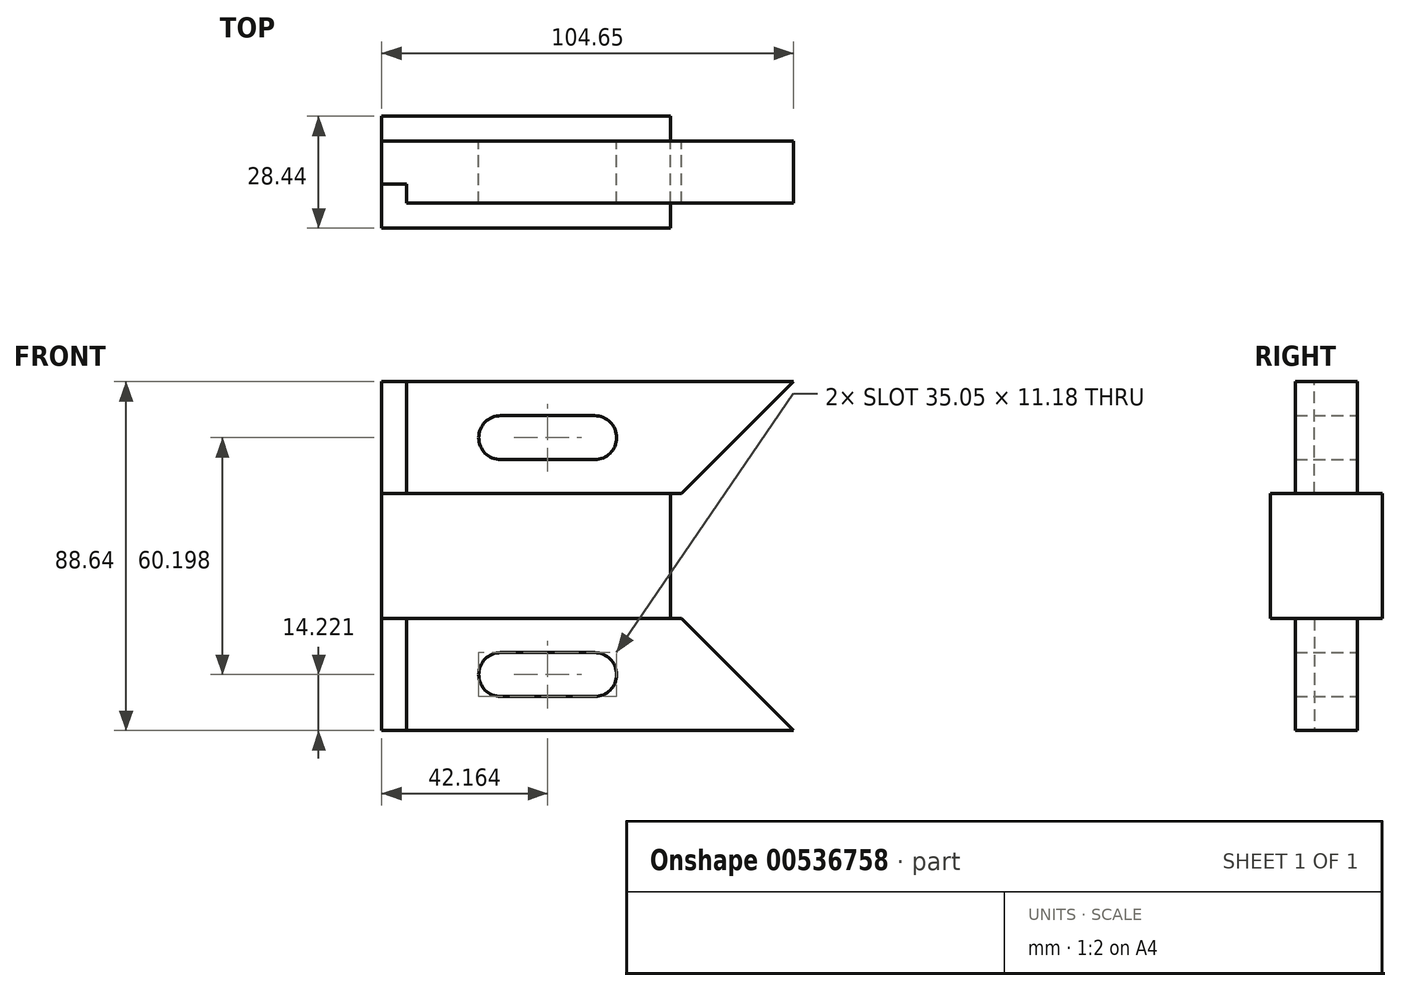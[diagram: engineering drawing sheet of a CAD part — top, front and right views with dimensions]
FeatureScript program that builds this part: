
annotation { "Feature Type Name" : "Feature", "Feature Type Description" : "" }
export const myFeature = defineFeature(function(context is Context, id is Id, definition is map)
    precondition{}
    {
        {
            var Q0;
            Q0=qCreatedBy(makeId("Right.planeOp"),FACE);
            var sketch = newSketch(context, id + "F0", { "sketchPlane" : qUnion([Q0])});
            skLineSegment(sketch, "E0.bottom", {"start": v(-14.22, 15.88) * mm, "end": v(14.22, 15.88) * mm});
            skLineSegment(sketch, "E0.top", {"start": v(-14.22, -15.87) * mm, "end": v(14.22, -15.87) * mm});
            skLineSegment(sketch, "E0.left", {"start": v(-14.22, 15.88) * mm, "end": v(-14.22, -15.88) * mm});
            skLineSegment(sketch, "E0.right", {"start": v(14.22, 15.88) * mm, "end": v(14.22, -15.88) * mm});
            skPoint(sketch, "E0.middle", {"position": v(0, 0) * mm});
            skSolve(sketch);
        }
        {
            var Q0;
            Q0=makeQuery(id+"F0.imprint","IMPRINT",FACE,{"disambiguationData":[TD([[makeQuery(id+"F0.imprint","IMPRINT",EDGE,{"derivedFrom":sQuery(id+"F0.wireOp",EDGE,"E0.bottom")}),-1.0]])]});
            extrude(context, id + "F1", {"entities" : qUnion([Q0]), "depth" : 73.4 * mm, "offsetDistance" : 25.4 * mm});
        }
        {
            var Q0;
            Q0=qCreatedBy(makeId("Front.planeOp"),FACE);
            var sketch = newSketch(context, id + "F2", { "sketchPlane" : qUnion([Q0])});
            skLineSegment(sketch, "E1.0", {"start": v(73.4, 15.88) * mm, "end": v(0, 15.88) * mm});
            skLineSegment(sketch, "E2", {"start": v(0, 15.88) * mm, "end": v(0, 44.32) * mm});
            skLineSegment(sketch, "E3", {"start": v(0, 44.32) * mm, "end": v(104.65, 44.32) * mm});
            skLineSegment(sketch, "E4", {"start": v(104.65, 44.32) * mm, "end": v(76.2, 15.88) * mm});
            skLineSegment(sketch, "E5", {"start": v(76.2, 15.87) * mm, "end": v(73.4, 15.88) * mm});
            skCircle(sketch, "E6", {"center": v(30.23, 30.1) * mm, "radius": 5.59 * mm});
            skCircle(sketch, "E7", {"center": v(54.1, 30.1) * mm, "radius": 5.59 * mm});
            skLineSegment(sketch, "E8", {"start": v(30.23, 35.69) * mm, "end": v(54.1, 35.69) * mm});
            skLineSegment(sketch, "E9", {"start": v(30.23, 24.51) * mm, "end": v(54.1, 24.51) * mm});
            skCircle(sketch, "E10.MirrorC", {"center": v(30.23, -30.1) * mm, "radius": 5.59 * mm});
            skCircle(sketch, "E11.MirrorC", {"center": v(54.1, -30.1) * mm, "radius": 5.59 * mm});
            skLineSegment(sketch, "E12.MirrorCS", {"start": v(104.65, -44.32) * mm, "end": v(76.2, -15.88) * mm});
            skLineSegment(sketch, "E13.MirrorCS", {"start": v(30.23, -35.69) * mm, "end": v(54.1, -35.69) * mm});
            skLineSegment(sketch, "E14.MirrorCS", {"start": v(0, -44.32) * mm, "end": v(104.65, -44.32) * mm});
            skLineSegment(sketch, "E15.MirrorCS", {"start": v(0, -15.88) * mm, "end": v(0, -44.32) * mm});
            skLineSegment(sketch, "E16.MirrorCS", {"start": v(73.4, -15.88) * mm, "end": v(0, -15.88) * mm});
            skLineSegment(sketch, "E17.MirrorCS", {"start": v(76.2, -15.87) * mm, "end": v(73.4, -15.88) * mm});
            skLineSegment(sketch, "E18.MirrorCS", {"start": v(30.23, -24.51) * mm, "end": v(54.1, -24.51) * mm});
            skSolve(sketch);
        }
        {
            var Q0;
            Q0=makeQuery(id+"F2.imprint","IMPRINT",FACE,{"disambiguationData":[TD([[makeQuery(id+"F2.imprint","IMPRINT",EDGE,{"derivedFrom":sQuery(id+"F2.wireOp",EDGE,"E12.MirrorCS")}),1.0]])]});
            var Q1;
            Q1=makeQuery(id+"F2.imprint","IMPRINT",FACE,{"disambiguationData":[TD([[makeQuery(id+"F2.imprint","IMPRINT",EDGE,{"derivedFrom":sQuery(id+"F2.wireOp",EDGE,"E1.0")}),-1.0]])]});
            extrude(context, id + "F3", {"entities" : qUnion([Q0, Q1]), "operationType" : NewBodyOperationType.ADD, "endBound" : BoundingType.SYMMETRIC, "depth" : 15.75 * mm, "offsetDistance" : 25.4 * mm});
        }
        {
            var Q0;
            Q0=makeQuery(id+"F3.opExtrude","CAP_FACE",FACE,{"disambiguationData":[OSD([sQuery(id+"F2.wireOp",EDGE,"E1.0"),sQuery(id+"F2.wireOp",EDGE,"E2"),sQuery(id+"F2.wireOp",EDGE,"E3"),sQuery(id+"F2.wireOp",EDGE,"E4"),sQuery(id+"F2.wireOp",EDGE,"E5"),sQuery(id+"F2.wireOp",EDGE,"E6"),sQuery(id+"F2.wireOp",EDGE,"E7"),sQuery(id+"F2.wireOp",EDGE,"E8"),sQuery(id+"F2.wireOp",EDGE,"E9")])],"isStart":false});
            var sketch = newSketch(context, id + "F4", { "sketchPlane" : qUnion([Q0])});
            skLineSegment(sketch, "E19.0.0", {"start": v(73.4, 15.88) * mm, "end": v(76.2, 15.87) * mm});
            skLineSegment(sketch, "E19.0.1", {"start": v(76.2, 15.88) * mm, "end": v(104.65, 44.32) * mm});
            skLineSegment(sketch, "E19.0.2", {"start": v(104.65, 44.32) * mm, "end": v(0, 44.32) * mm});
            skLineSegment(sketch, "E19.0.3", {"start": v(0, 44.32) * mm, "end": v(0, 15.88) * mm});
            skLineSegment(sketch, "E19.0.4", {"start": v(0, 15.88) * mm, "end": v(73.4, 15.88) * mm});
            skLineSegment(sketch, "E20", {"start": v(104.65, 44.32) * mm, "end": v(69.6, 44.32) * mm});
            skLineSegment(sketch, "E21", {"start": v(69.6, 44.32) * mm, "end": v(69.6, 26.8) * mm});
            skLineSegment(sketch, "E22", {"start": v(69.6, 26.8) * mm, "end": v(87.12, 26.8) * mm});
            skSolve(sketch);
        }
        {
            var Q0;
            {var subQ1=sQuery(id+"F4.wireOp",EDGE,"E19.0.0");Q0=makeQuery(id+"F4.imprint","IMPRINT",FACE,{"disambiguationData":[TD([[makeQuery(id+"F4.imprint","IMPRINT",EDGE,{"derivedFrom":subQ1}),-1.0]])]});}
            var sketch = newSketch(context, id + "F5", { "sketchPlane" : qUnion([Q0])});
            skLineSegment(sketch, "E23.0", {"start": v(0, 44.32) * mm, "end": v(0, 15.88) * mm});
            skLineSegment(sketch, "E24.0", {"start": v(0, 15.88) * mm, "end": v(73.4, 15.88) * mm});
            skLineSegment(sketch, "E25.bottom", {"start": v(0, 44.32) * mm, "end": v(6.35, 44.32) * mm});
            skLineSegment(sketch, "E25.top", {"start": v(0, 15.88) * mm, "end": v(6.35, 15.88) * mm});
            skLineSegment(sketch, "E25.right", {"start": v(6.35, 44.32) * mm, "end": v(6.35, 15.88) * mm});
            skLineSegment(sketch, "E26.MirrorCS", {"start": v(6.35, -44.32) * mm, "end": v(6.35, -15.88) * mm});
            skLineSegment(sketch, "E27.MirrorCS", {"start": v(0, -15.88) * mm, "end": v(6.35, -15.88) * mm});
            skLineSegment(sketch, "E28.MirrorCS", {"start": v(0, -44.32) * mm, "end": v(0, -15.88) * mm});
            skLineSegment(sketch, "E29.MirrorCS", {"start": v(0, -44.32) * mm, "end": v(6.35, -44.32) * mm});
            skSolve(sketch);
        }
        {
            var Q0;
            Q0=makeQuery(id+"F5.imprint","IMPRINT",FACE,{"disambiguationData":[TD([[makeQuery(id+"F5.imprint","IMPRINT",EDGE,{"derivedFrom":sQuery(id+"F5.wireOp",EDGE,"E25.bottom")}),-1.0]])]});
            extrude(context, id + "F6", {"entities" : qUnion([Q0]), "operationType" : NewBodyOperationType.REMOVE, "oppositeDirection" : true, "depth" : 4.83 * mm, "offsetDistance" : 25.4 * mm});
        }
        {
            var Q0;
            Q0=makeQuery(id+"F3.opExtrude","CAP_FACE",FACE,{"disambiguationData":[OSD([sQuery(id+"F2.wireOp",EDGE,"E10.MirrorC"),sQuery(id+"F2.wireOp",EDGE,"E11.MirrorC"),sQuery(id+"F2.wireOp",EDGE,"E12.MirrorCS"),sQuery(id+"F2.wireOp",EDGE,"E13.MirrorCS"),sQuery(id+"F2.wireOp",EDGE,"E14.MirrorCS"),sQuery(id+"F2.wireOp",EDGE,"E15.MirrorCS"),sQuery(id+"F2.wireOp",EDGE,"E16.MirrorCS"),sQuery(id+"F2.wireOp",EDGE,"E17.MirrorCS"),sQuery(id+"F2.wireOp",EDGE,"E18.MirrorCS")])],"isStart":false});
            var sketch = newSketch(context, id + "F7", { "sketchPlane" : qUnion([Q0])});
            skLineSegment(sketch, "E30.bottom", {"start": v(0, -44.32) * mm, "end": v(6.35, -44.32) * mm});
            skLineSegment(sketch, "E30.top", {"start": v(0, -15.88) * mm, "end": v(6.35, -15.88) * mm});
            skLineSegment(sketch, "E30.left", {"start": v(0, -44.32) * mm, "end": v(0, -15.88) * mm});
            skLineSegment(sketch, "E30.right", {"start": v(6.35, -44.32) * mm, "end": v(6.35, -15.88) * mm});
            skSolve(sketch);
        }
        {
            var Q0;
            Q0=makeQuery(id+"F7.imprint","IMPRINT",FACE,{"disambiguationData":[TD([[makeQuery(id+"F7.imprint","IMPRINT",EDGE,{"derivedFrom":sQuery(id+"F7.wireOp",EDGE,"E30.bottom")}),1.0]])]});
            extrude(context, id + "F8", {"entities" : qUnion([Q0]), "operationType" : NewBodyOperationType.REMOVE, "oppositeDirection" : true, "depth" : 4.83 * mm, "offsetDistance" : 25.4 * mm});
        }
    });
